# Revit family: EL_Emergency-Lighting-Inverter_Myers_Illuminator EM
name_source: partatom
category: Electrical Equipment
units: mm (PartAtom-declared; Revit-internal decimal feet)

## family parameters
Cut with Voids When Loaded = No
Host = Face
Maintain Annotation Orientation = No
Part Type = Other Panel
Room Calculation Point = No
Round Connector Dimension = Use Diameter
Shared = No

## types (4) — shared parameters
CLEARANCE FRONT = 3' - 0"
CLEARANCE SIDE = 0' - 2"
CLEARANCE TOP = 0' - 6"
DEPTH = 0' - 10 1/2"
Default Elevation = 0' - 0"
Description = Emergency Lighting Inverter
Manufacturer = Myers
SHARED REMARK TYPE = For floor mount: option -F. For wall-mount use option -W.
SHARED SPECIFICATION = 26 50 00 - Lighting
Type Comments = Emergency Lighting Inverter
URL = www.myerseps.com
WIDTH = 2' - 0 1/4"

## per-type parameters (varying)
| type | HEIGHT INVERTER | Model | SHARED APPARENT POWER | SHARED TYPE MARK | SHARED WEIGHT |
| ELI-2.8kVA | 4' - 7" | EM-4-S-B-10-05-T-M(BBM)-I | 2800 VA | EI-2.8 KVA | 603.00 lbf |
| ELI-1.6kVA | 3' - 7 1/4" | EM-2-S-B-10-03-T-M(BBM)-I | 1600 VA | EI-1.6 KVA | 405.00 lbf |
| ELI-2.2kVA | 3' - 7 1/4" | EM-3-S-B-10-04-T-M(BBM)-I | 2200 VA | EI-2.2 KVA | 494.00 lbf |
| ELI-1.0kVA | 2' - 3 1/2" | EM-1-S-B-10-02-T-M(BBM)-I | 1000 VA | EI-1 KVA | 281.00 lbf |

## geometry (parser evidence)
native form markers: Blend x4, Sweep x1
no freeform markers — native parametric forms only
